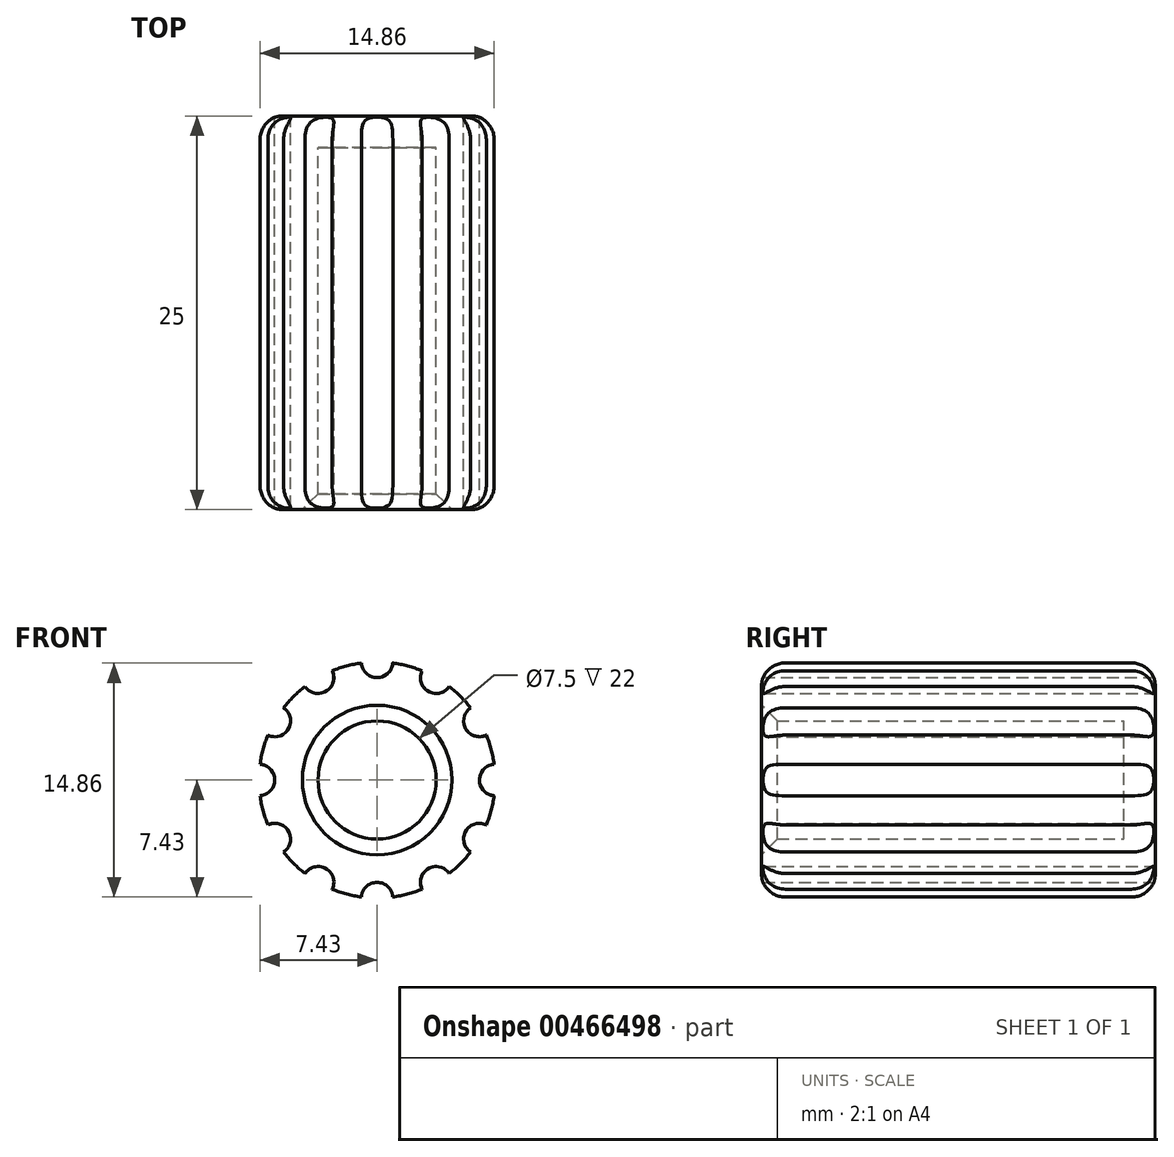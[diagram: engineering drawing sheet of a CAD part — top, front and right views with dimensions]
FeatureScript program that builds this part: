
annotation { "Feature Type Name" : "Feature", "Feature Type Description" : "" }
export const myFeature = defineFeature(function(context is Context, id is Id, definition is map)
    precondition{}
    {
        {
            var Q0;
            Q0=qCreatedBy(makeId("Front.planeOp"),FACE);
            var sketch = newSketch(context, id + "F0", { "sketchPlane" : qUnion([Q0])});
            skCircle(sketch, "E0", {"center": v(0, 0) * mm, "radius": 3.75 * mm});
            skCircle(sketch, "E1", {"center": v(0, 0) * mm, "radius": 7.5 * mm});
            skSolve(sketch);
        }
        {
            var Q0;
            Q0 = qSketchRegion(id + "F0", true);
            extrude(context, id + "F1", {"entities" : qUnion([Q0]), "depth" : 25 * mm});
        }
        {
            var Q0;
            Q0=makeQuery(id+"F0.imprint","IMPRINT",FACE,{"disambiguationData":[TD([[makeQuery(id+"F0.imprint","IMPRINT",EDGE,{"derivedFrom":sQuery(id+"F0.wireOp",EDGE,"E0")}),1.0]])]});
            extrude(context, id + "F2", {"entities" : qUnion([Q0]), "operationType" : NewBodyOperationType.ADD, "depth" : 2 * mm});
        }
        {
            var Q0;
            Q0=makeQuery(id+"F0.imprint","IMPRINT",FACE,{"disambiguationData":[TD([[makeQuery(id+"F0.imprint","IMPRINT",EDGE,{"derivedFrom":sQuery(id+"F0.wireOp",EDGE,"E0")}),-1.0]])]});
            var sketch = newSketch(context, id + "F3", { "sketchPlane" : qUnion([Q0])});
            skCircle(sketch, "E2", {"center": v(0, 7.5) * mm, "radius": 1 * mm});
            skCircle(sketch, "E3.1.0", {"center": v(-3.75, 6.5) * mm, "radius": 1 * mm});
            skCircle(sketch, "E3.2.0", {"center": v(-6.5, 3.75) * mm, "radius": 1 * mm});
            skCircle(sketch, "E3.3.0", {"center": v(-7.5, 0) * mm, "radius": 1 * mm});
            skCircle(sketch, "E3.4.0", {"center": v(-6.5, -3.75) * mm, "radius": 1 * mm});
            skCircle(sketch, "E3.5.0", {"center": v(-3.75, -6.5) * mm, "radius": 1 * mm});
            skCircle(sketch, "E3.6.0", {"center": v(0, -7.5) * mm, "radius": 1 * mm});
            skCircle(sketch, "E3.7.0", {"center": v(3.75, -6.5) * mm, "radius": 1 * mm});
            skCircle(sketch, "E3.8.0", {"center": v(6.5, -3.75) * mm, "radius": 1 * mm});
            skCircle(sketch, "E3.9.0", {"center": v(7.5, 0) * mm, "radius": 1 * mm});
            skCircle(sketch, "E3.10.0", {"center": v(6.5, 3.75) * mm, "radius": 1 * mm});
            skCircle(sketch, "E3.11.0", {"center": v(3.75, 6.5) * mm, "radius": 1 * mm});
            skPoint(sketch, "E3.center", {"position": v(0, 0) * mm});
            skSolve(sketch);
        }
        {
            var Q0;
            Q0=makeQuery(id+"F1.opExtrude","CAP_EDGE",EDGE,{"disambiguationData":[OSD([sQuery(id+"F0.wireOp",EDGE,"E1")])],"isStart":true});
            fillet(context, id + "F4", {"entities" : qUnion([Q0]), "radius" : 1.5 * mm, "tangentPropagation" : true, "allowEdgeOverflow" : false});
        }
        {
            var Q0;
            Q0=makeQuery(id+"F1.opExtrude","CAP_EDGE",EDGE,{"disambiguationData":[OSD([sQuery(id+"F0.wireOp",EDGE,"E1")])],"isStart":false});
            fillet(context, id + "F5", {"entities" : qUnion([Q0]), "radius" : 1.5 * mm, "tangentPropagation" : true, "allowEdgeOverflow" : false});
        }
        {
            var Q0;
            {var subQ0=sQuery(id+"F3.wireOp",EDGE,"E2");var subQ1=makeQuery(id+"F0.imprint","IMPRINT",EDGE,{"derivedFrom":sQuery(id+"F0.wireOp",EDGE,"E1")});var subQ2=makeQuery(id+"F3.imprint","INTERSECT",VERTEX,{"disambiguationData":[OD(0.0)],"derivedFrom":[subQ1,subQ0]});Q0=makeQuery(id+"F3.imprint","IMPRINT",FACE,{"disambiguationData":[TD([[makeQuery(id+"F3.imprint","IMPRINT",EDGE,{"disambiguationData":[TD([[subQ2,-1.0]])],"derivedFrom":subQ0}),1.0]])]});}
            var Q1;
            {var subQ0=sQuery(id+"F3.wireOp",EDGE,"E3.11.0");var subQ1=makeQuery(id+"F0.imprint","IMPRINT",EDGE,{"derivedFrom":sQuery(id+"F0.wireOp",EDGE,"E1")});var subQ2=makeQuery(id+"F3.imprint","INTERSECT",VERTEX,{"disambiguationData":[OD(0.0)],"derivedFrom":[subQ1,subQ0]});Q1=makeQuery(id+"F3.imprint","IMPRINT",FACE,{"disambiguationData":[TD([[makeQuery(id+"F3.imprint","IMPRINT",EDGE,{"disambiguationData":[TD([[subQ2,-1.0]])],"derivedFrom":subQ0}),1.0]])]});}
            var Q2;
            {var subQ0=sQuery(id+"F3.wireOp",EDGE,"E3.10.0");var subQ1=makeQuery(id+"F0.imprint","IMPRINT",EDGE,{"derivedFrom":sQuery(id+"F0.wireOp",EDGE,"E1")});var subQ2=makeQuery(id+"F3.imprint","INTERSECT",VERTEX,{"disambiguationData":[OD(0.0)],"derivedFrom":[subQ1,subQ0]});Q2=makeQuery(id+"F3.imprint","IMPRINT",FACE,{"disambiguationData":[TD([[makeQuery(id+"F3.imprint","IMPRINT",EDGE,{"disambiguationData":[TD([[subQ2,-1.0]])],"derivedFrom":subQ0}),1.0]])]});}
            var Q3;
            {var subQ0=sQuery(id+"F3.wireOp",EDGE,"E3.9.0");var subQ1=makeQuery(id+"F0.imprint","IMPRINT",EDGE,{"derivedFrom":sQuery(id+"F0.wireOp",EDGE,"E1")});var subQ2=makeQuery(id+"F3.imprint","INTERSECT",VERTEX,{"disambiguationData":[OD(0.0)],"derivedFrom":[subQ1,subQ0]});Q3=makeQuery(id+"F3.imprint","IMPRINT",FACE,{"disambiguationData":[TD([[makeQuery(id+"F3.imprint","IMPRINT",EDGE,{"disambiguationData":[TD([[subQ2,1.0]])],"derivedFrom":subQ0}),1.0]])]});}
            var Q4;
            {var subQ0=sQuery(id+"F3.wireOp",EDGE,"E3.8.0");var subQ1=makeQuery(id+"F0.imprint","IMPRINT",EDGE,{"derivedFrom":sQuery(id+"F0.wireOp",EDGE,"E1")});var subQ2=makeQuery(id+"F3.imprint","INTERSECT",VERTEX,{"disambiguationData":[OD(0.0)],"derivedFrom":[subQ1,subQ0]});Q4=makeQuery(id+"F3.imprint","IMPRINT",FACE,{"disambiguationData":[TD([[makeQuery(id+"F3.imprint","IMPRINT",EDGE,{"disambiguationData":[TD([[subQ2,1.0]])],"derivedFrom":subQ0}),1.0]])]});}
            var Q5;
            {var subQ0=sQuery(id+"F3.wireOp",EDGE,"E3.7.0");var subQ1=makeQuery(id+"F0.imprint","IMPRINT",EDGE,{"derivedFrom":sQuery(id+"F0.wireOp",EDGE,"E1")});var subQ2=makeQuery(id+"F3.imprint","INTERSECT",VERTEX,{"disambiguationData":[OD(0.0)],"derivedFrom":[subQ1,subQ0]});Q5=makeQuery(id+"F3.imprint","IMPRINT",FACE,{"disambiguationData":[TD([[makeQuery(id+"F3.imprint","IMPRINT",EDGE,{"disambiguationData":[TD([[subQ2,1.0]])],"derivedFrom":subQ0}),1.0]])]});}
            var Q6;
            {var subQ0=sQuery(id+"F3.wireOp",EDGE,"E3.6.0");var subQ1=makeQuery(id+"F0.imprint","IMPRINT",EDGE,{"derivedFrom":sQuery(id+"F0.wireOp",EDGE,"E1")});var subQ2=makeQuery(id+"F3.imprint","INTERSECT",VERTEX,{"disambiguationData":[OD(0.0)],"derivedFrom":[subQ1,subQ0]});Q6=makeQuery(id+"F3.imprint","IMPRINT",FACE,{"disambiguationData":[TD([[makeQuery(id+"F3.imprint","IMPRINT",EDGE,{"disambiguationData":[TD([[subQ2,1.0]])],"derivedFrom":subQ0}),1.0]])]});}
            var Q7;
            {var subQ0=sQuery(id+"F3.wireOp",EDGE,"E3.5.0");var subQ1=makeQuery(id+"F0.imprint","IMPRINT",EDGE,{"derivedFrom":sQuery(id+"F0.wireOp",EDGE,"E1")});var subQ2=makeQuery(id+"F3.imprint","INTERSECT",VERTEX,{"disambiguationData":[OD(0.0)],"derivedFrom":[subQ1,subQ0]});Q7=makeQuery(id+"F3.imprint","IMPRINT",FACE,{"disambiguationData":[TD([[makeQuery(id+"F3.imprint","IMPRINT",EDGE,{"disambiguationData":[TD([[subQ2,1.0]])],"derivedFrom":subQ0}),1.0]])]});}
            var Q8;
            {var subQ0=sQuery(id+"F3.wireOp",EDGE,"E3.4.0");var subQ1=makeQuery(id+"F0.imprint","IMPRINT",EDGE,{"derivedFrom":sQuery(id+"F0.wireOp",EDGE,"E1")});var subQ2=makeQuery(id+"F3.imprint","INTERSECT",VERTEX,{"disambiguationData":[OD(0.0)],"derivedFrom":[subQ1,subQ0]});Q8=makeQuery(id+"F3.imprint","IMPRINT",FACE,{"disambiguationData":[TD([[makeQuery(id+"F3.imprint","IMPRINT",EDGE,{"disambiguationData":[TD([[subQ2,1.0]])],"derivedFrom":subQ0}),1.0]])]});}
            var Q9;
            {var subQ0=sQuery(id+"F3.wireOp",EDGE,"E3.3.0");var subQ1=makeQuery(id+"F0.imprint","IMPRINT",EDGE,{"derivedFrom":sQuery(id+"F0.wireOp",EDGE,"E1")});var subQ2=makeQuery(id+"F3.imprint","INTERSECT",VERTEX,{"disambiguationData":[OD(0.0)],"derivedFrom":[subQ1,subQ0]});Q9=makeQuery(id+"F3.imprint","IMPRINT",FACE,{"disambiguationData":[TD([[makeQuery(id+"F3.imprint","IMPRINT",EDGE,{"disambiguationData":[TD([[subQ2,-1.0]])],"derivedFrom":subQ0}),1.0]])]});}
            var Q10;
            {var subQ0=sQuery(id+"F3.wireOp",EDGE,"E3.2.0");var subQ1=makeQuery(id+"F0.imprint","IMPRINT",EDGE,{"derivedFrom":sQuery(id+"F0.wireOp",EDGE,"E1")});var subQ2=makeQuery(id+"F3.imprint","INTERSECT",VERTEX,{"disambiguationData":[OD(0.0)],"derivedFrom":[subQ1,subQ0]});Q10=makeQuery(id+"F3.imprint","IMPRINT",FACE,{"disambiguationData":[TD([[makeQuery(id+"F3.imprint","IMPRINT",EDGE,{"disambiguationData":[TD([[subQ2,-1.0]])],"derivedFrom":subQ0}),1.0]])]});}
            var Q11;
            {var subQ0=sQuery(id+"F3.wireOp",EDGE,"E3.1.0");var subQ1=makeQuery(id+"F0.imprint","IMPRINT",EDGE,{"derivedFrom":sQuery(id+"F0.wireOp",EDGE,"E1")});var subQ2=makeQuery(id+"F3.imprint","INTERSECT",VERTEX,{"disambiguationData":[OD(0.0)],"derivedFrom":[subQ1,subQ0]});Q11=makeQuery(id+"F3.imprint","IMPRINT",FACE,{"disambiguationData":[TD([[makeQuery(id+"F3.imprint","IMPRINT",EDGE,{"disambiguationData":[TD([[subQ2,-1.0]])],"derivedFrom":subQ0}),1.0]])]});}
            extrude(context, id + "F6", {"entities" : qUnion([Q0, Q1, Q2, Q3, Q4, Q5, Q6, Q7, Q8, Q9, Q10, Q11]), "operationType" : NewBodyOperationType.REMOVE, "depth" : 25 * mm});
        }
        {
            var Q0;
            Q0=makeQuery(id+"F1.opExtrude","CAP_EDGE",EDGE,{"disambiguationData":[OSD([sQuery(id+"F0.wireOp",EDGE,"E0")])],"isStart":false});
            chamfer(context, id + "F7", {"entities" : qUnion([Q0]), "width" : 1 * mm, "tangentPropagation" : true});
        }
    });
